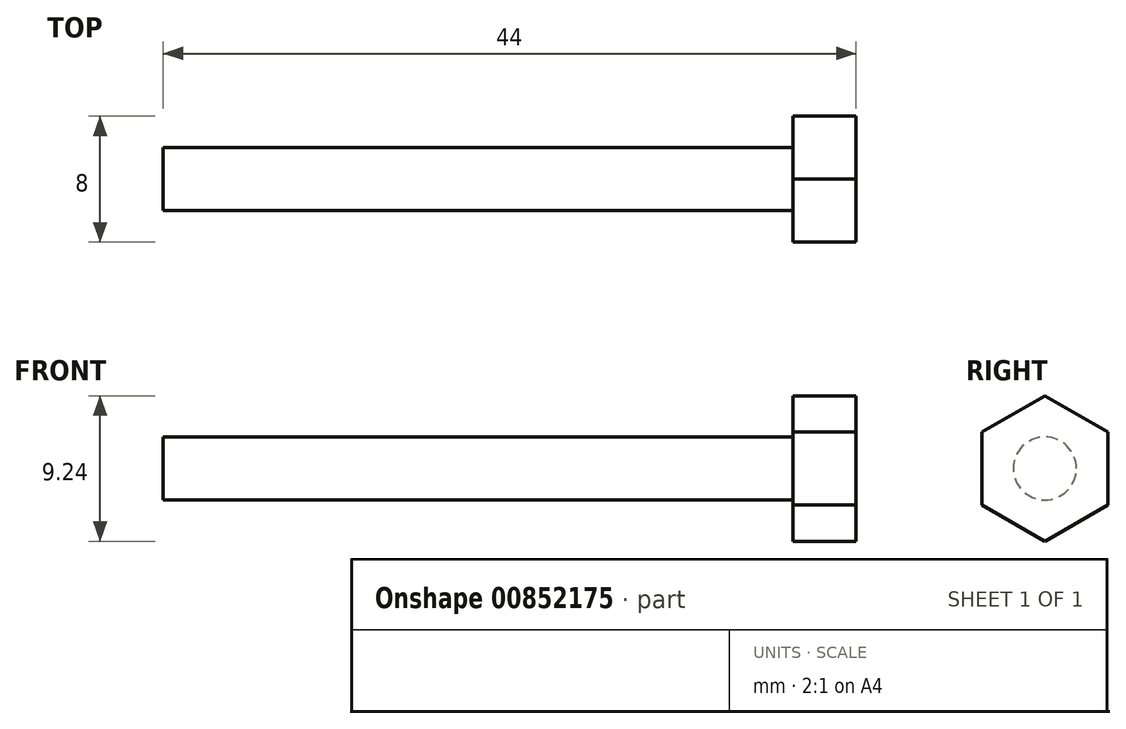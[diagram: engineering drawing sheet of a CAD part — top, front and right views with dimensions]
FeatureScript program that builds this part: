
annotation { "Feature Type Name" : "Feature", "Feature Type Description" : "" }
export const myFeature = defineFeature(function(context is Context, id is Id, definition is map)
    precondition{}
    {
        {
            var Q0;
            Q0=qCreatedBy(makeId("Right.planeOp"),FACE);
            var sketch = newSketch(context, id + "F0", { "sketchPlane" : qUnion([Q0])});
            skCircle(sketch, "E0", {"center": v(0, 0) * mm, "radius": 2 * mm});
            skSolve(sketch);
        }
        {
            var Q0;
            Q0 = qSketchRegion(id + "F0", true);
            extrude(context, id + "F1", {"entities" : qUnion([Q0]), "oppositeDirection" : true, "depth" : 40 * mm, "offsetDistance" : 25 * mm});
        }
        {
            var Q0;
            Q0=makeQuery(id+"F1.opExtrude","CAP_FACE",FACE,{"disambiguationData":[OSD([sQuery(id+"F0.wireOp",EDGE,"E0")])],"isStart":true});
            var sketch = newSketch(context, id + "F2", { "sketchPlane" : qUnion([Q0])});
            skCircle(sketch, "E1.cCircle", {"center": v(0, 0) * mm, "radius": 4 * mm, "construction": true});
            skLineSegment(sketch, "E1.0", {"start": v(4, 2.3) * mm, "end": v(4, -2.3) * mm});
            skLineSegment(sketch, "E1.1", {"start": v(4, -2.3) * mm, "end": v(0, -4.62) * mm});
            skLineSegment(sketch, "E1.2", {"start": v(0, -4.62) * mm, "end": v(-4, -2.3) * mm});
            skLineSegment(sketch, "E1.3", {"start": v(-4, -2.3) * mm, "end": v(-4, 2.3) * mm});
            skLineSegment(sketch, "E1.4", {"start": v(-4, 2.3) * mm, "end": v(0, 4.62) * mm});
            skLineSegment(sketch, "E1.5", {"start": v(0, 4.62) * mm, "end": v(4, 2.3) * mm});
            skPoint(sketch, "E1.0.midPoint", {"position": v(4, 0) * mm});
            skSolve(sketch);
        }
        {
            var Q0;
            Q0 = qSketchRegion(id + "F2", true);
            extrude(context, id + "F3", {"entities" : qUnion([Q0]), "operationType" : NewBodyOperationType.ADD, "depth" : 4 * mm, "offsetDistance" : 25 * mm});
        }
    });
